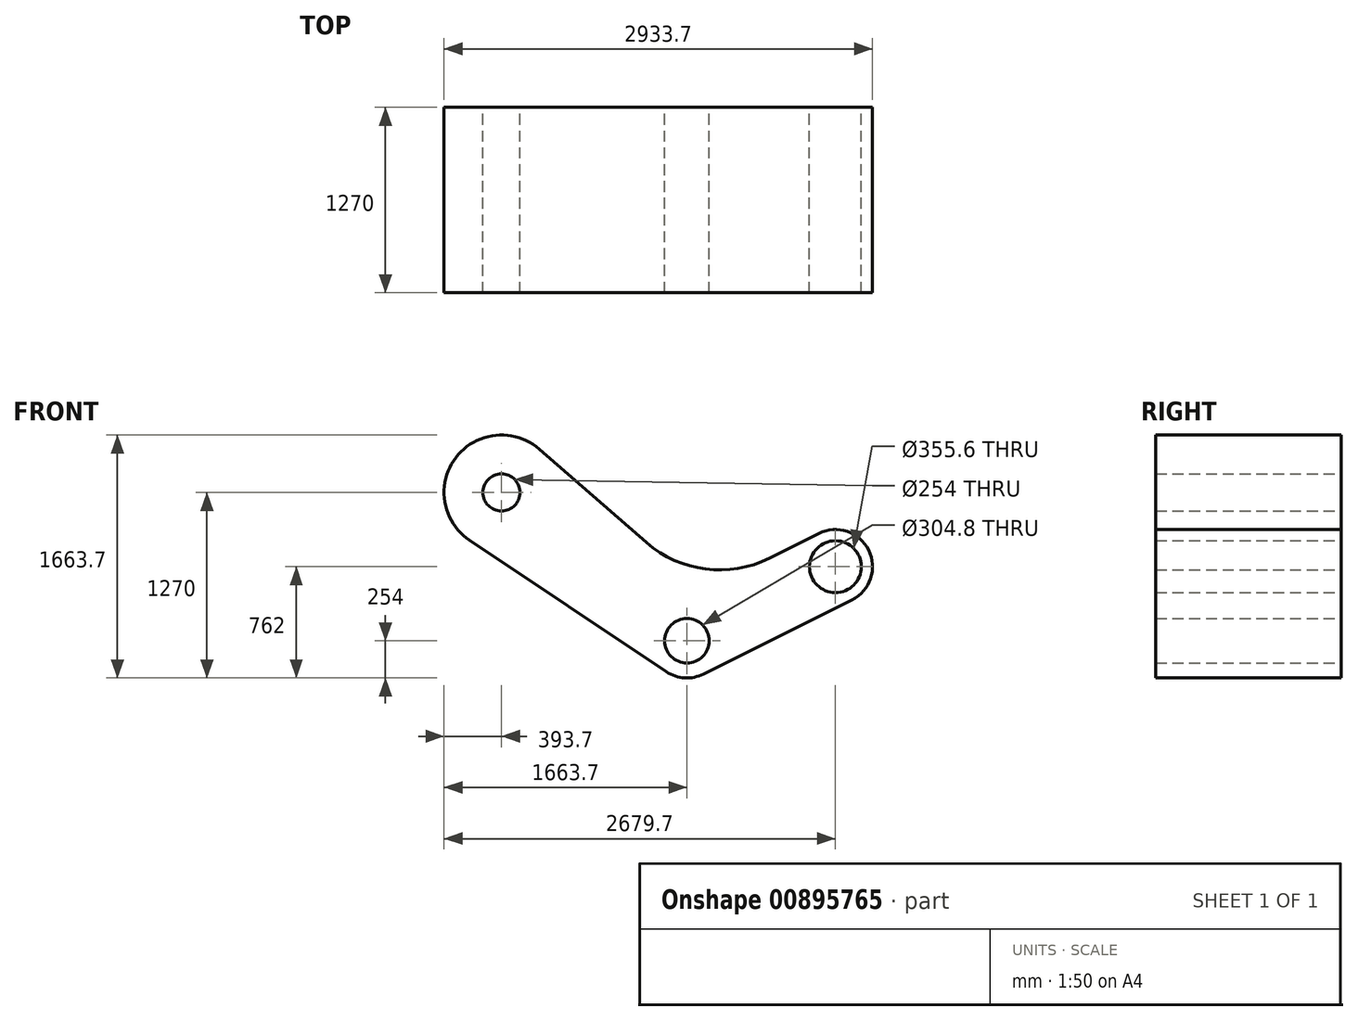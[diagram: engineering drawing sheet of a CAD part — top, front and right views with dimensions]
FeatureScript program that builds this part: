
annotation { "Feature Type Name" : "Feature", "Feature Type Description" : "" }
export const myFeature = defineFeature(function(context is Context, id is Id, definition is map)
    precondition{}
    {
        {
            var Q0;
            Q0=qCreatedBy(makeId("Front.planeOp"),FACE);
            var sketch = newSketch(context, id + "F0", { "sketchPlane" : qUnion([Q0])});
            skCircle(sketch, "E0", {"center": v(0, 0) * mm, "radius": 254 * mm});
            skCircle(sketch, "E1", {"center": v(0, 0) * mm, "radius": 152.4 * mm});
            skCircle(sketch, "E2", {"center": v(-1270, 1016) * mm, "radius": 393.7 * mm});
            skCircle(sketch, "E3", {"center": v(-1270, 1016) * mm, "radius": 127 * mm});
            skCircle(sketch, "E4", {"center": v(1016, 508) * mm, "radius": 254 * mm});
            skCircle(sketch, "E5", {"center": v(1016, 508) * mm, "radius": 177.8 * mm});
            skLineSegment(sketch, "E6", {"start": v(-1488.63, 688.58) * mm, "end": v(-141.05, -211.24) * mm});
            skLineSegment(sketch, "E7", {"start": v(-1011.46, 1312.91) * mm, "end": v(-276.68, 673.1) * mm});
            skLineSegment(sketch, "E8", {"start": v(564.49, 566.23) * mm, "end": v(902.4, 735.18) * mm});
            skLineSegment(sketch, "E9", {"start": v(113.6, -227.18) * mm, "end": v(1129.6, 280.82) * mm});
            skPoint(sketch, "E10.visualSharp", {"position": v(108.12, 338.04) * mm});
            skArc(sketch, "E10.filletArc", {"start": v(-276.68, 673.1) * mm, "mid": v(127.66, 491.86) * mm, "end": v(564.49, 566.23) * mm});
            skSolve(sketch);
        }
        {
            var Q0;
            Q0=makeQuery(id+"F0.imprint","IMPRINT",FACE,{"disambiguationData":[TD([[makeQuery(id+"F0.imprint","IMPRINT",EDGE,{"derivedFrom":sQuery(id+"F0.wireOp",EDGE,"E3")}),-1.0]])]});
            var Q1;
            {var subQ0=sQuery(id+"F0.wireOp",EDGE,"E6");Q1=makeQuery(id+"F0.imprint","IMPRINT",FACE,{"disambiguationData":[TD([[makeQuery(id+"F0.imprint","IMPRINT",EDGE,{"derivedFrom":subQ0}),1.0]])]});}
            var Q2;
            Q2=makeQuery(id+"F0.imprint","IMPRINT",FACE,{"disambiguationData":[TD([[makeQuery(id+"F0.imprint","IMPRINT",EDGE,{"derivedFrom":sQuery(id+"F0.wireOp",EDGE,"E1")}),-1.0]])]});
            var Q3;
            Q3=makeQuery(id+"F0.imprint","IMPRINT",FACE,{"disambiguationData":[TD([[makeQuery(id+"F0.imprint","IMPRINT",EDGE,{"derivedFrom":sQuery(id+"F0.wireOp",EDGE,"E5")}),-1.0]])]});
            extrude(context, id + "F1", {"entities" : qUnion([Q0, Q1, Q2, Q3]), "endBound" : BoundingType.SYMMETRIC, "depth" : 1270 * mm, "offsetDistance" : 25.4 * mm});
        }
    });
